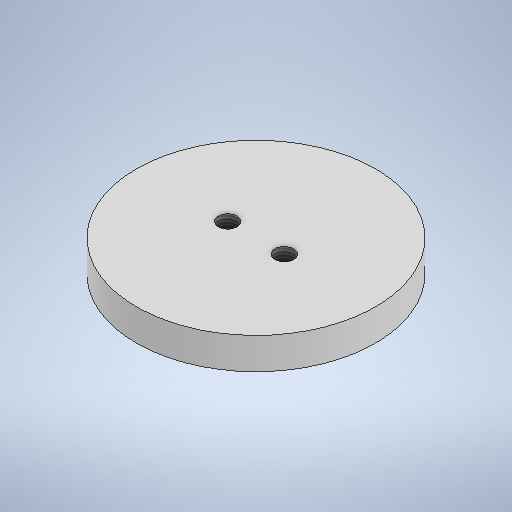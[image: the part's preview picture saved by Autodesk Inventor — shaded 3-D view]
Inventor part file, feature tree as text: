
AUTODESK INVENTOR PART (.ipt)
format: ipt  version: 2025.2 (Build 292293000, 293)  size: 230,400 bytes
history: native  units: in
note: dims shown in document units (in); Inventor stores cm internally (conversion verified against a paired STEP export)
features: extrude x3, sketch x2, thread x2
ambient origin geometry x8: Origin, YZ Plane, XZ Plane, XY Plane, X Axis, Y Axis, Z Axis, Center Point
bodies: Solid1 (feature_tree)
feature tree (7):
  extrude  "Extrusion1"  Depth=0.1969in TaperAngle=0.0deg
  sketch  "Sketch2"  dims[d5=0.1181in d6=0.1181in d7=0.1969in d8=0.0in d9=0.1969in d10=0.0in d11=0.1969in d12=0.0in d13=0.1969in d14=0.0in]
  extrude  "Extrusion2"  Depth=0.1969in
  extrude  "Extrusion3"  Depth=0.1969in TaperAngle=0.0deg
  thread  "Thread1"  [1 undecoded]
  thread  "Thread2"  [1 undecoded]
  sketch  "Sketch1"  dims[d0=1.4961in d1=0.1969in d2=0.0in]
note: 2 required parameter values undecoded (feature->parameter linkage not recoverable at this tier; creation-order binding heuristic only, values carry confidence <= 0.55)
